# Revit family: Casement_38_G_Top_Hung_Standard
name_source: partatom
category: Windows
revit_build: Autodesk Revit 2014 (Build: 20130308_1515(x64)
units: mm (PartAtom-declared; Revit-internal decimal feet)

## types (12) — shared parameters
Aluminium Thickness = 1 mm  [stored 0.00328084 ft]
Bead SG Gap = 13 mm  [stored 0.0426509 ft]
Bottom Hung = No
Casement Dimension = 38 mm  [stored 0.124672 ft]
Custom Sash Height Bottom = 569 mm  [stored 1.8668 ft]
Custom Sash Height Top = 569 mm  [stored 1.8668 ft]
Custom Window Height = 1190 mm  [stored 3.9042 ft]
DG Extrusion Start = 9 mm  [stored 0.0295276 ft]
DG Gasket Finish = Double Glazing Gasket Material
DG Thickness Calc = 4 mm  [stored 0.0131234 ft]
Default Sill Height = 800 mm  [stored 2.62467 ft]
Depth Bead = 24 mm  [stored 0.0787402 ft]
Description = Window 38mm, Type G top hung
Frame Center Offset = 19 mm  [stored 0.062336 ft]
Height = 1200 mm  [stored 3.93701 ft]
Height Panel 1 = 555 mm  [stored 1.82087 ft]
Height Panel 2 = 555 mm  [stored 1.82087 ft]
Height Panel 4 = 1140 mm  [stored 3.74016 ft]
Height Sash 1 = 539 mm
Height Sash 2 = 539 mm
Height Sash Bottom Opening = 569 mm  [stored 1.8668 ft]
Height Sash Top Opening = 569 mm  [stored 1.8668 ft]
Length Mullion = 1200 mm  [stored 3.93701 ft]
Limit Fixed Pane Height Max = 1800 mm
Limit Fixed Pane Height Min = 200 mm  [stored 0.656168 ft]
Limit Fixed Pane Width Max = 1500 mm
Limit Fixed Pane Width Min = 200 mm  [stored 0.656168 ft]
Limit Sash Bottom Height Max Based On Top Sash = 1229 mm
Limit Sash Height Bottom Max = 1200 mm  [stored 3.93701 ft]
Limit Sash Height Bottom Min = 300 mm  [stored 0.984252 ft]
Limit Sash Height Top Max = 1200 mm  [stored 3.93701 ft]
Limit Sash Height Top Min = 300 mm  [stored 0.984252 ft]
Limit Sash Width Max = 1500 mm
Limit Sash Width Min = 300 mm  [stored 0.984252 ft]
Limit Window Height Max = 1860 mm
Manufacturer = Crealco
Max System DG One Piece Thickness = 6 mm  [stored 0.019685 ft]
Max System DG Unit Thickness = 25 mm  [stored 0.082021 ft]
Model = Casement 38
Offset Bead SG Center Reversed = 19 mm  [stored 0.062336 ft]
Offset Sash 1 Top = 23 mm  [stored 0.0754593 ft]
Offset Sash 2 Top = 608 mm  [stored 1.99475 ft]
Offset Sash Left = 23 mm  [stored 0.0754593 ft]
Offset Transom 1 Top = 585 mm  [stored 1.91929 ft]
Offset Window Exterior = 19 mm  [stored 0.062336 ft]
Rough Width = 16 mm  [stored 0.0524934 ft]
SG Gasket Thickness = 6 mm  [stored 0.019685 ft]
Sash Center Offset = 16 mm  [stored 0.0524934 ft]
Sash Overlap = 7 mm  [stored 0.0229659 ft]
Sash Spacing Inner = 8 mm  [stored 0.0262467 ft]
Top Hung = Yes
URL = http://www.crealco.co.za
Wall Closure = By host
Width Bead = 15 mm  [stored 0.0492126 ft]
Width Profile = 30 mm  [stored 0.0984252 ft]
zero-valued in all types: Window Exterior Offset

## per-type parameters (varying)
- 38-1212DT-1000Pa: Area Pane Left Bottom=0.25 m²; Area Pane Left Top=0.25 m²; Area Pane Right=0.6 m²; Clearvue Insulated LowE SHGC Value=0.652; Clearvue Insulated LowE U Value=4.72; Clearvue Insulated SHGC Value=0.716; Clearvue Insulated U Value=5.41; Clearvue SHGC Value=0.827; Clearvue U Value=8.31; Custom Sash Width=569 mm  [stored 1.8668 ft]; Custom Windload=1000 mm  [stored 3.28084 ft]; Custom Window Width=1190 mm  [stored 3.9042 ft]; Depth Mullion=39 mm  [stored 0.127953 ft]; Energy Advantage SHGC Value=0.741; Energy Advantage U Value=6.28; Intruderprufe Insulated LowE SHGC Value=0.606; Intruderprufe Insulated LowE U Value=4.62; Intruderprufe Insulated SHGC Value=0.665; Intruderprufe Insulated U Value=5.28; Intruderprufe LowE SHGC Value=0.688; Intruderprufe LowE U Value=6.14; Intruderprufe SHGC Value=0.801; Intruderprufe U Value=8.22; Length Transom=555 mm  [stored 1.82087 ft]; Limit Window Width Max=2145 mm; Limit Window Width Min=845 mm  [stored 2.77231 ft]; Max Pane Area=0.6 m²; Mullion Depth Windload Based=39 mm  [stored 0.127953 ft]; Offset Mullion Left=585 mm  [stored 1.91929 ft]; Offset Panel 4 Left=615 mm  [stored 2.01772 ft]; Width=1190 mm  [stored 3.9042 ft]; Width Panel 1=555 mm  [stored 1.82087 ft]; Width Panel 2=555 mm  [stored 1.82087 ft]; Width Panel 4=545 mm; Width Sash 1=539 mm; Width Sash 2=539 mm; Width Sash Opening=569 mm  [stored 1.8668 ft]; Windload Design=1000 mm  [stored 3.28084 ft]
- 38-1212DT-1500Pa: Area Pane Left Bottom=0.25 m²; Area Pane Left Top=0.25 m²; Area Pane Right=0.6 m²; Clearvue Insulated LowE SHGC Value=0.652; Clearvue Insulated LowE U Value=4.72; Clearvue Insulated SHGC Value=0.716; Clearvue Insulated U Value=5.41; Clearvue SHGC Value=0.827; Clearvue U Value=8.31; Custom Sash Width=569 mm  [stored 1.8668 ft]; Custom Windload=1500 mm; Custom Window Width=1190 mm  [stored 3.9042 ft]; Depth Mullion=39 mm  [stored 0.127953 ft]; Energy Advantage SHGC Value=0.741; Energy Advantage U Value=6.28; Intruderprufe Insulated LowE SHGC Value=0.606; Intruderprufe Insulated LowE U Value=4.62; Intruderprufe Insulated SHGC Value=0.665; Intruderprufe Insulated U Value=5.28; Intruderprufe LowE SHGC Value=0.688; Intruderprufe LowE U Value=6.14; Intruderprufe SHGC Value=0.801; Intruderprufe U Value=8.22; Length Transom=555 mm  [stored 1.82087 ft]; Limit Window Width Max=2145 mm; Limit Window Width Min=845 mm  [stored 2.77231 ft]; Max Pane Area=0.6 m²; Mullion Depth Windload Based=39 mm  [stored 0.127953 ft]; Offset Mullion Left=585 mm  [stored 1.91929 ft]; Offset Panel 4 Left=615 mm  [stored 2.01772 ft]; Width=1190 mm  [stored 3.9042 ft]; Width Panel 1=555 mm  [stored 1.82087 ft]; Width Panel 2=555 mm  [stored 1.82087 ft]; Width Panel 4=545 mm; Width Sash 1=539 mm; Width Sash 2=539 mm; Width Sash Opening=569 mm  [stored 1.8668 ft]; Windload Design=1500 mm
- 38-1212DT-2000Pa: Area Pane Left Bottom=0.25 m²; Area Pane Left Top=0.25 m²; Area Pane Right=0.6 m²; Clearvue Insulated LowE SHGC Value=0.652; Clearvue Insulated LowE U Value=4.72; Clearvue Insulated SHGC Value=0.716; Clearvue Insulated U Value=5.41; Clearvue SHGC Value=0.827; Clearvue U Value=8.31; Custom Sash Width=569 mm  [stored 1.8668 ft]; Custom Windload=2000 mm; Custom Window Width=1190 mm  [stored 3.9042 ft]; Depth Mullion=39 mm  [stored 0.127953 ft]; Energy Advantage SHGC Value=0.741; Energy Advantage U Value=6.28; Intruderprufe Insulated LowE SHGC Value=0.606; Intruderprufe Insulated LowE U Value=4.62; Intruderprufe Insulated SHGC Value=0.665; Intruderprufe Insulated U Value=5.28; Intruderprufe LowE SHGC Value=0.688; Intruderprufe LowE U Value=6.14; Intruderprufe SHGC Value=0.801; Intruderprufe U Value=8.22; Length Transom=555 mm  [stored 1.82087 ft]; Limit Window Width Max=2145 mm; Limit Window Width Min=845 mm  [stored 2.77231 ft]; Max Pane Area=0.6 m²; Mullion Depth Windload Based=39 mm  [stored 0.127953 ft]; Offset Mullion Left=585 mm  [stored 1.91929 ft]; Offset Panel 4 Left=615 mm  [stored 2.01772 ft]; Width=1190 mm  [stored 3.9042 ft]; Width Panel 1=555 mm  [stored 1.82087 ft]; Width Panel 2=555 mm  [stored 1.82087 ft]; Width Panel 4=545 mm; Width Sash 1=539 mm; Width Sash 2=539 mm; Width Sash Opening=569 mm  [stored 1.8668 ft]; Windload Design=2000 mm
- 38-1512DT-1000Pa: Area Pane Left Bottom=0.25 m²; Area Pane Left Top=0.25 m²; Area Pane Right=0.94 m²; Clearvue Insulated LowE SHGC Value=0.74; Clearvue Insulated LowE U Value=4.72; Clearvue Insulated SHGC Value=0.813; Clearvue Insulated U Value=5.52; Clearvue SHGC Value=0.936; Clearvue U Value=8.83; Custom Sash Width=569 mm  [stored 1.8668 ft]; Custom Windload=1000 mm  [stored 3.28084 ft]; Custom Window Width=1490 mm; Depth Mullion=39 mm  [stored 0.127953 ft]; Energy Advantage SHGC Value=0.838; Energy Advantage U Value=6.52; Intruderprufe Insulated LowE SHGC Value=0.686; Intruderprufe Insulated LowE U Value=4.63; Intruderprufe Insulated SHGC Value=0.755; Intruderprufe Insulated U Value=5.39; Intruderprufe LowE SHGC Value=0.778; Intruderprufe LowE U Value=6.38; Intruderprufe SHGC Value=0.9; Intruderprufe U Value=8.72; Length Transom=555 mm  [stored 1.82087 ft]; Limit Window Width Max=2145 mm; Limit Window Width Min=845 mm  [stored 2.77231 ft]; Max Pane Area=0.94 m²; Mullion Depth Windload Based=39 mm  [stored 0.127953 ft]; Offset Mullion Left=585 mm  [stored 1.91929 ft]; Offset Panel 4 Left=615 mm  [stored 2.01772 ft]; Width=1490 mm; Width Panel 1=555 mm  [stored 1.82087 ft]; Width Panel 2=555 mm  [stored 1.82087 ft]; Width Panel 4=845 mm  [stored 2.77231 ft]; Width Sash 1=539 mm; Width Sash 2=539 mm; Width Sash Opening=569 mm  [stored 1.8668 ft]; Windload Design=1000 mm  [stored 3.28084 ft]
- 38-1512DT-1500Pa: Area Pane Left Bottom=0.25 m²; Area Pane Left Top=0.25 m²; Area Pane Right=0.94 m²; Clearvue Insulated LowE SHGC Value=0.74; Clearvue Insulated LowE U Value=4.72; Clearvue Insulated SHGC Value=0.813; Clearvue Insulated U Value=5.52; Clearvue SHGC Value=0.936; Clearvue U Value=8.83; Custom Sash Width=569 mm  [stored 1.8668 ft]; Custom Windload=1500 mm; Custom Window Width=1490 mm; Depth Mullion=39 mm  [stored 0.127953 ft]; Energy Advantage SHGC Value=0.838; Energy Advantage U Value=6.52; Intruderprufe Insulated LowE SHGC Value=0.686; Intruderprufe Insulated LowE U Value=4.63; Intruderprufe Insulated SHGC Value=0.755; Intruderprufe Insulated U Value=5.39; Intruderprufe LowE SHGC Value=0.778; Intruderprufe LowE U Value=6.38; Intruderprufe SHGC Value=0.9; Intruderprufe U Value=8.72; Length Transom=555 mm  [stored 1.82087 ft]; Limit Window Width Max=2145 mm; Limit Window Width Min=845 mm  [stored 2.77231 ft]; Max Pane Area=0.94 m²; Mullion Depth Windload Based=39 mm  [stored 0.127953 ft]; Offset Mullion Left=585 mm  [stored 1.91929 ft]; Offset Panel 4 Left=615 mm  [stored 2.01772 ft]; Width=1490 mm; Width Panel 1=555 mm  [stored 1.82087 ft]; Width Panel 2=555 mm  [stored 1.82087 ft]; Width Panel 4=845 mm  [stored 2.77231 ft]; Width Sash 1=539 mm; Width Sash 2=539 mm; Width Sash Opening=569 mm  [stored 1.8668 ft]; Windload Design=1500 mm
- 38-1812DT-1000Pa: Area Pane Left Bottom=0.39 m²; Area Pane Left Top=0.39 m²; Area Pane Right=0.96 m²; Clearvue Insulated LowE SHGC Value=0.696; Clearvue Insulated LowE U Value=4.35; Clearvue Insulated SHGC Value=0.765; Clearvue Insulated U Value=5.11; Clearvue SHGC Value=0.882; Clearvue U Value=8.22; Custom Sash Width=854 mm  [stored 2.80184 ft]; Custom Windload=1000 mm  [stored 3.28084 ft]; Custom Window Width=1790 mm; Depth Mullion=39 mm  [stored 0.127953 ft]; Energy Advantage SHGC Value=0.79; Energy Advantage U Value=6.04; Intruderprufe Insulated LowE SHGC Value=0.645; Intruderprufe Insulated LowE U Value=4.26; Intruderprufe Insulated SHGC Value=0.71; Intruderprufe Insulated U Value=4.99; Intruderprufe LowE SHGC Value=0.732; Intruderprufe LowE U Value=5.91; Intruderprufe SHGC Value=0.849; Intruderprufe U Value=8.14; Length Transom=840 mm  [stored 2.75591 ft]; Limit Window Width Max=2430 mm; Limit Window Width Min=1130 mm  [stored 3.70735 ft]; Max Pane Area=0.96 m²; Mullion Depth Windload Based=39 mm  [stored 0.127953 ft]; Offset Mullion Left=870 mm  [stored 2.85433 ft]; Offset Panel 4 Left=900 mm  [stored 2.95276 ft]; Width=1790 mm; Width Panel 1=840 mm  [stored 2.75591 ft]; Width Panel 2=840 mm  [stored 2.75591 ft]; Width Panel 4=860 mm; Width Sash 1=824 mm; Width Sash 2=824 mm; Width Sash Opening=854 mm  [stored 2.80184 ft]; Windload Design=1000 mm  [stored 3.28084 ft]
- 38-1512DT-2000Pa: Area Pane Left Bottom=0.25 m²; Area Pane Left Top=0.25 m²; Area Pane Right=0.94 m²; Clearvue Insulated LowE SHGC Value=0.741; Clearvue Insulated LowE U Value=4.77; Clearvue Insulated SHGC Value=0.814; Clearvue Insulated U Value=5.57; Clearvue SHGC Value=0.935; Clearvue U Value=8.83; Custom Sash Width=569 mm  [stored 1.8668 ft]; Custom Windload=2000 mm; Custom Window Width=1490 mm; Depth Mullion=54 mm  [stored 0.177165 ft]; Energy Advantage SHGC Value=0.837; Energy Advantage U Value=6.58; Intruderprufe Insulated LowE SHGC Value=0.687; Intruderprufe Insulated LowE U Value=4.68; Intruderprufe Insulated SHGC Value=0.757; Intruderprufe Insulated U Value=5.44; Intruderprufe LowE SHGC Value=0.78; Intruderprufe LowE U Value=6.44; Intruderprufe SHGC Value=0.889; Intruderprufe U Value=8.74; Length Transom=555 mm  [stored 1.82087 ft]; Limit Window Width Max=2145 mm; Limit Window Width Min=845 mm  [stored 2.77231 ft]; Max Pane Area=0.94 m²; Mullion Depth Windload Based=54 mm  [stored 0.177165 ft]; Offset Mullion Left=585 mm  [stored 1.91929 ft]; Offset Panel 4 Left=615 mm  [stored 2.01772 ft]; Width=1490 mm; Width Panel 1=555 mm  [stored 1.82087 ft]; Width Panel 2=555 mm  [stored 1.82087 ft]; Width Panel 4=845 mm  [stored 2.77231 ft]; Width Sash 1=539 mm; Width Sash 2=539 mm; Width Sash Opening=569 mm  [stored 1.8668 ft]; Windload Design=2000 mm
- 38-1812DT-1500Pa: Area Pane Left Bottom=0.39 m²; Area Pane Left Top=0.39 m²; Area Pane Right=0.96 m²; Clearvue Insulated LowE SHGC Value=0.696; Clearvue Insulated LowE U Value=4.35; Clearvue Insulated SHGC Value=0.765; Clearvue Insulated U Value=5.11; Clearvue SHGC Value=0.882; Clearvue U Value=8.22; Custom Sash Width=854 mm  [stored 2.80184 ft]; Custom Windload=1500 mm; Custom Window Width=1790 mm; Depth Mullion=39 mm  [stored 0.127953 ft]; Energy Advantage SHGC Value=0.79; Energy Advantage U Value=6.04; Intruderprufe Insulated LowE SHGC Value=0.645; Intruderprufe Insulated LowE U Value=4.26; Intruderprufe Insulated SHGC Value=0.71; Intruderprufe Insulated U Value=4.99; Intruderprufe LowE SHGC Value=0.732; Intruderprufe LowE U Value=5.91; Intruderprufe SHGC Value=0.849; Intruderprufe U Value=8.14; Length Transom=840 mm  [stored 2.75591 ft]; Limit Window Width Max=2430 mm; Limit Window Width Min=1130 mm  [stored 3.70735 ft]; Max Pane Area=0.96 m²; Mullion Depth Windload Based=39 mm  [stored 0.127953 ft]; Offset Mullion Left=870 mm  [stored 2.85433 ft]; Offset Panel 4 Left=900 mm  [stored 2.95276 ft]; Width=1790 mm; Width Panel 1=840 mm  [stored 2.75591 ft]; Width Panel 2=840 mm  [stored 2.75591 ft]; Width Panel 4=860 mm; Width Sash 1=824 mm; Width Sash 2=824 mm; Width Sash Opening=854 mm  [stored 2.80184 ft]; Windload Design=1500 mm
- 38-1812DT-2000Pa: Area Pane Left Bottom=0.39 m²; Area Pane Left Top=0.39 m²; Area Pane Right=0.96 m²; Clearvue Insulated LowE SHGC Value=0.698; Clearvue Insulated LowE U Value=4.45; Clearvue Insulated SHGC Value=0.766; Clearvue Insulated U Value=5.21; Clearvue SHGC Value=0.882; Clearvue U Value=8.16; Custom Sash Width=854 mm  [stored 2.80184 ft]; Custom Windload=2000 mm; Custom Window Width=1790 mm; Depth Mullion=54 mm  [stored 0.177165 ft]; Energy Advantage SHGC Value=0.79; Energy Advantage U Value=6.17; Intruderprufe Insulated LowE SHGC Value=0.646; Intruderprufe Insulated LowE U Value=4.36; Intruderprufe Insulated SHGC Value=0.711; Intruderprufe Insulated U Value=5.08; Intruderprufe LowE SHGC Value=0.733; Intruderprufe LowE U Value=6.04; Intruderprufe SHGC Value=0.833; Intruderprufe U Value=8.16; Length Transom=840 mm  [stored 2.75591 ft]; Limit Window Width Max=2430 mm; Limit Window Width Min=1130 mm  [stored 3.70735 ft]; Max Pane Area=0.96 m²; Mullion Depth Windload Based=54 mm  [stored 0.177165 ft]; Offset Mullion Left=870 mm  [stored 2.85433 ft]; Offset Panel 4 Left=900 mm  [stored 2.95276 ft]; Width=1790 mm; Width Panel 1=840 mm  [stored 2.75591 ft]; Width Panel 2=840 mm  [stored 2.75591 ft]; Width Panel 4=860 mm; Width Sash 1=824 mm; Width Sash 2=824 mm; Width Sash Opening=854 mm  [stored 2.80184 ft]; Windload Design=2000 mm
- 38-2412DT-1000Pa: Area Pane Left Bottom=0.39 m²; Area Pane Left Top=0.39 m²; Area Pane Right=1.64 m²; Clearvue Insulated LowE SHGC Value=0.549; Clearvue Insulated LowE U Value=3; Clearvue Insulated SHGC Value=0.604; Clearvue Insulated U Value=3.61; Clearvue SHGC Value=0; Clearvue U Value=7.9; Custom Sash Width=854 mm  [stored 2.80184 ft]; Custom Windload=1000 mm  [stored 3.28084 ft]; Custom Window Width=2390 mm; Depth Mullion=39 mm  [stored 0.127953 ft]; Energy Advantage SHGC Value=0; Energy Advantage U Value=7.9; Intruderprufe Insulated LowE SHGC Value=0.508; Intruderprufe Insulated LowE U Value=2.95; Intruderprufe Insulated SHGC Value=0.56; Intruderprufe Insulated U Value=3.53; Intruderprufe LowE SHGC Value=0.576; Intruderprufe LowE U Value=4.27; Intruderprufe SHGC Value=0.665; Intruderprufe U Value=6.01; Length Transom=840 mm  [stored 2.75591 ft]; Limit Window Width Max=2430 mm; Limit Window Width Min=1130 mm  [stored 3.70735 ft]; Max Pane Area=1.64 m²; Mullion Depth Windload Based=39 mm  [stored 0.127953 ft]; Offset Mullion Left=870 mm  [stored 2.85433 ft]; Offset Panel 4 Left=900 mm  [stored 2.95276 ft]; Width=2390 mm; Width Panel 1=840 mm  [stored 2.75591 ft]; Width Panel 2=840 mm  [stored 2.75591 ft]; Width Panel 4=1460 mm; Width Sash 1=824 mm; Width Sash 2=824 mm; Width Sash Opening=854 mm  [stored 2.80184 ft]; Windload Design=1000 mm  [stored 3.28084 ft]
- 38-2412DT-1500Pa: Area Pane Left Bottom=0.39 m²; Area Pane Left Top=0.39 m²; Area Pane Right=1.64 m²; Clearvue Insulated LowE SHGC Value=0.55; Clearvue Insulated LowE U Value=3.03; Clearvue Insulated SHGC Value=0.604; Clearvue Insulated U Value=3.64; Clearvue SHGC Value=0; Clearvue U Value=7.9; Custom Sash Width=854 mm  [stored 2.80184 ft]; Custom Windload=1500 mm; Custom Window Width=2390 mm; Depth Mullion=54 mm  [stored 0.177165 ft]; Energy Advantage SHGC Value=0; Energy Advantage U Value=7.9; Intruderprufe Insulated LowE SHGC Value=0.508; Intruderprufe Insulated LowE U Value=2.97; Intruderprufe Insulated SHGC Value=0.561; Intruderprufe Insulated U Value=3.56; Intruderprufe LowE SHGC Value=0.577; Intruderprufe LowE U Value=4.3; Intruderprufe SHGC Value=0.659; Intruderprufe U Value=6.02; Length Transom=840 mm  [stored 2.75591 ft]; Limit Window Width Max=2430 mm; Limit Window Width Min=1130 mm  [stored 3.70735 ft]; Max Pane Area=1.64 m²; Mullion Depth Windload Based=54 mm  [stored 0.177165 ft]; Offset Mullion Left=870 mm  [stored 2.85433 ft]; Offset Panel 4 Left=900 mm  [stored 2.95276 ft]; Width=2390 mm; Width Panel 1=840 mm  [stored 2.75591 ft]; Width Panel 2=840 mm  [stored 2.75591 ft]; Width Panel 4=1460 mm; Width Sash 1=824 mm; Width Sash 2=824 mm; Width Sash Opening=854 mm  [stored 2.80184 ft]; Windload Design=1500 mm
- 38-2412DT-2000Pa: Area Pane Left Bottom=0.39 m²; Area Pane Left Top=0.39 m²; Area Pane Right=1.64 m²; Clearvue Insulated LowE SHGC Value=0.55; Clearvue Insulated LowE U Value=3.03; Clearvue Insulated SHGC Value=0.604; Clearvue Insulated U Value=3.64; Clearvue SHGC Value=0; Clearvue U Value=7.9; Custom Sash Width=854 mm  [stored 2.80184 ft]; Custom Windload=2000 mm; Custom Window Width=2390 mm; Depth Mullion=54 mm  [stored 0.177165 ft]; Energy Advantage SHGC Value=0; Energy Advantage U Value=7.9; Intruderprufe Insulated LowE SHGC Value=0.508; Intruderprufe Insulated LowE U Value=2.97; Intruderprufe Insulated SHGC Value=0.561; Intruderprufe Insulated U Value=3.56; Intruderprufe LowE SHGC Value=0.577; Intruderprufe LowE U Value=4.3; Intruderprufe SHGC Value=0.659; Intruderprufe U Value=6.02; Length Transom=840 mm  [stored 2.75591 ft]; Limit Window Width Max=2430 mm; Limit Window Width Min=1130 mm  [stored 3.70735 ft]; Max Pane Area=1.64 m²; Mullion Depth Windload Based=54 mm  [stored 0.177165 ft]; Offset Mullion Left=870 mm  [stored 2.85433 ft]; Offset Panel 4 Left=900 mm  [stored 2.95276 ft]; Width=2390 mm; Width Panel 1=840 mm  [stored 2.75591 ft]; Width Panel 2=840 mm  [stored 2.75591 ft]; Width Panel 4=1460 mm; Width Sash 1=824 mm; Width Sash 2=824 mm; Width Sash Opening=854 mm  [stored 2.80184 ft]; Windload Design=2000 mm

note: [stored X ft] marks values corroborated as IEEE doubles in the binary element streams (Revit-internal decimal feet)

## geometry (parser evidence)
native form markers: Blend x4, Extrusion x1, Sweep x28
no freeform markers — native parametric forms only
